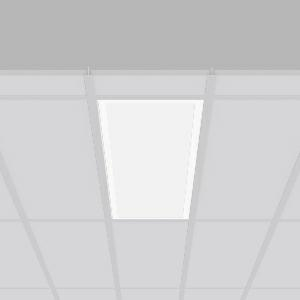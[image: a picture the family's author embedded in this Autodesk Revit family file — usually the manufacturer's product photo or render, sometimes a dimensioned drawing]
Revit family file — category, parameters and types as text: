
# Revit family: sidelite_eco_312367_002_1_790_03ba
name_source: partatom
category: Lighting Fixtures
units: mm (PartAtom-declared; Revit-internal decimal feet)

## family parameters
Cut with Voids When Loaded = No
Host = Face
Light Source = No
Part Type = Normal
Room Calculation Point = No
Round Connector Dimension = Use Diameter
Shared = No

## types (1)
- MultiLumen 1 (1 x LED Modul 840, 3500 lm, 4000)
    Apparent Load = 29 VA
    CIE Flux Codes = 47 79 96 100 100
    Color Rendering = 80
    Color Temperature = 4000
    Default Elevation = 1800 mm
    Description = Series: SIDELITE ECO
Highly economical recessed luminaire with progressive LED technology. Frame made of aluminium, powder-coated. Diffuser: plastic, opal. Lightguide and diffuser made of non-yellowing plastic (PMMA). Lateral light emission (RZB SIDELITE technology) for homogeneous light distribution. External driver. External driver with simple plug-in locking system and extended converter connecting cable to luminaire (1.90 m). MultiLumen: 4 steps adjustable luminous flux. Factory setting is the lowest offered step. Luminaire can be used with accessories (to be ordered separately) as recessed or surface mounting luminaire. Qualified for use in the food and drink industry. 
Colour: white
Length: 1245 mm
Width: 308 mm
Cut-out length: 1233 mm
Cut-out width: 296 mm
Recess height: 160 mm
Luminaire: recess height: 37 mm
Lamp: LED
Socket: without socket
Colour temperature: 4000K
Colour rendering index (CRI): 80
System power: 29 W
Rated luminous flux: 3500 lm
Luminous efficiency: 121 lm/W
System power 2: 33 W
Rated luminous flux 2: 3850 lm
Luminous efficiency 2: 117 lm/W
System power 3: 35 W
Rated luminous flux 3: 4050 lm
Luminous efficiency 3: 116 lm/W
System power 4: 38 W
Rated luminous flux 4: 4400 lm
Luminous efficiency 4: 116 lm/W
Control gear: Regulated power supply
Protection class: II
Type of protection: IP 40
    Height = 0 mm  [stored 0 ft]
    Lamp = 1 x LED Modul 840
    Lamp Light Flux = 3500 lm
    Lamp count = 1
    Length = 1245 mm
    Lifetime = 50000 h
    Luminous efficacy = 121 lm/W
    Manufacturer = RZB
    ModVariant = No
    Model = 312367.002.1.790
    Mounting Place = Ceiling
    Mounting Type = Recessed
    Number of Poles = 1
    OnlyDefault = Yes
    Power Factor = 1
    Product Name = SIDELITE ECO
    Product group = Recessed modular luminaires
    ProductGroupID = 406
    Protection Class = Protection class II
    Protection Degree = IP 20
    RLX_Detail_Level = 1
    RLX_Emergency_Light_Flux = 0 lm
    RLX_Emergency_Type = 0
    RLX_Emergency_Type_DB = No
    RlxData = <blob elided: 31481 chars, md5=0581e8d3>
    Socket = socket
    Standby Power = 0 W
    System Light Flux = 3500 lm
    System Power = 29 W
    Type Comments = MultiLumen 1
    Type Image = 312367.002.jpg
    URL = http://relux.com
    VarID = multilumen_1
    Voltage = 230 V
    Voltage Range = 220-240 V
    Weight = 0.00 kg
    Width = 308 mm

note: [stored X ft] marks values corroborated as IEEE doubles in the binary element streams (Revit-internal decimal feet)

## geometry (parser evidence)
native form markers: Blend x4, Sweep x10
no freeform markers — native parametric forms only
